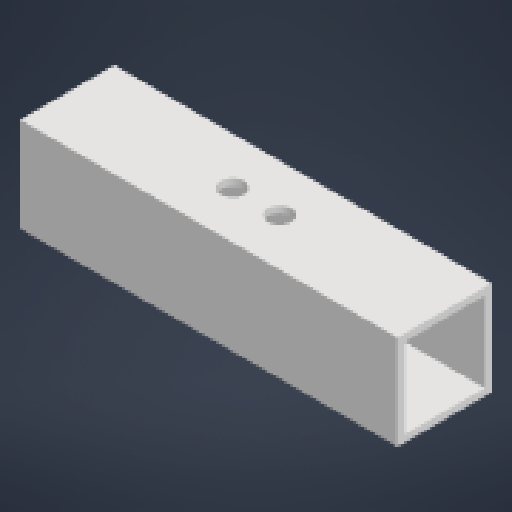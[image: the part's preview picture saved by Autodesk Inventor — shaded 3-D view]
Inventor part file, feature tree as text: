
AUTODESK INVENTOR PART (.ipt)
format: ipt  version: 2024 (Build 280153000, 153)  size: 151,040 bytes
history: native  units: mm
features: other x5, extrude x3, sketch x3, reference x2
ambient origin geometry x8: Origin, YZ Plane, XZ Plane, XY Plane, X Axis, Y Axis, Z Axis, Center Point
bodies: Body1 (feature_tree)
feature tree (13):
  other  "Твердое тело1"
  extrude  "Выдавливание1"  Depth=20.0mm
  extrude  "Выдавливание2"  Depth=1.5mm
  extrude  "Выдавливание3"  Depth=50.0mm TaperAngle=0.0deg
  sketch  "Эскиз1"
  reference  "Ссылка1"
  reference  "Ссылка2"
  sketch  "Эскиз3"
  sketch  "Эскиз4"
  parser-record x1  (decoder bookkeeping rows leaked as tree rows — omitted from the tree; the rows remain in map.json)
  other  "var1.iam"
  other  "DIN 7985 (H) M5x45-H:1"
  other  "DIN 7985 (H) M5x45-H:2"
note: 1 file-system path scrubbed to <path> (originals preserved in map.json)
